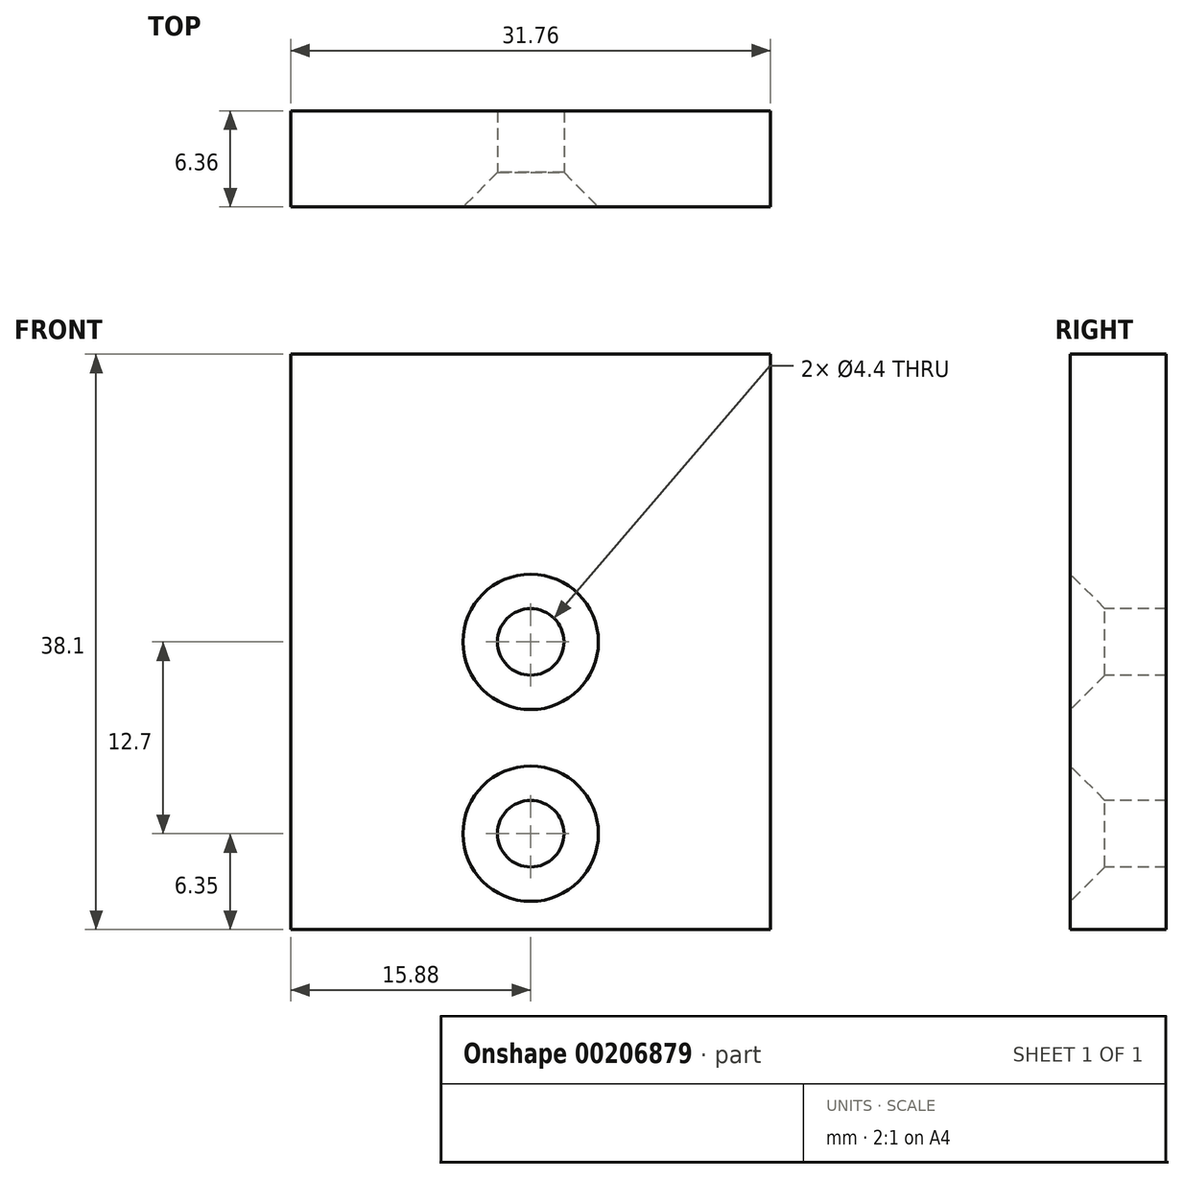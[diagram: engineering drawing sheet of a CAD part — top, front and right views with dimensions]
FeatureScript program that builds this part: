
annotation { "Feature Type Name" : "Feature", "Feature Type Description" : "" }
export const myFeature = defineFeature(function(context is Context, id is Id, definition is map)
    precondition{}
    {
        {
            var Q0;
            Q0=qCreatedBy(makeId("Front.planeOp"),FACE);
            var sketch = newSketch(context, id + "F0", { "sketchPlane" : qUnion([Q0])});
            skLineSegment(sketch, "E0.bottom", {"start": v(-15.87, 19.05) * mm, "end": v(15.88, 19.05) * mm});
            skLineSegment(sketch, "E0.top", {"start": v(-15.88, -19.05) * mm, "end": v(15.87, -19.05) * mm});
            skLineSegment(sketch, "E0.left", {"start": v(-15.87, 19.05) * mm, "end": v(-15.88, -19.05) * mm});
            skLineSegment(sketch, "E0.right", {"start": v(15.88, 19.05) * mm, "end": v(15.87, -19.05) * mm});
            skPoint(sketch, "E0.middle", {"position": v(0, 0) * mm});
            skSolve(sketch);
        }
        {
            var Q0;
            Q0=qSketchRegion(id+"F0",true);
            extrude(context, id + "F1", {"entities" : qUnion([Q0]), "endBound" : BoundingType.SYMMETRIC, "depth" : 6.35 * mm});
        }
        {
            var Q0;
            Q0=makeQuery(id+"F1.opExtrude","CAP_FACE",FACE,{"disambiguationData":[OSD([sQuery(id+"F0.wireOp",EDGE,"E0.bottom"),sQuery(id+"F0.wireOp",EDGE,"E0.top"),sQuery(id+"F0.wireOp",EDGE,"E0.left"),sQuery(id+"F0.wireOp",EDGE,"E0.right")])],"isStart":false});
            var sketch = newSketch(context, id + "F2", { "sketchPlane" : qUnion([Q0])});
            skPoint(sketch, "E1", {"position": v(0, -12.7) * mm});
            skPoint(sketch, "E2", {"position": v(0, 0) * mm});
            skSolve(sketch);
        }
        {
            var Q0;
            Q0=sQuery(id+"F2.wireOp",VERTEX,"E2");
            var Q1;
            Q1=sQuery(id+"F2.wireOp",VERTEX,"E1");
            var Q2;
            Q2=makeQuery(id+"F1.opExtrude","SWEPT_BODY",BODY,{"disambiguationData":[OSD([sQuery(id+"F0.wireOp",EDGE,"E0.bottom"),sQuery(id+"F0.wireOp",EDGE,"E0.top"),sQuery(id+"F0.wireOp",EDGE,"E0.left"),sQuery(id+"F0.wireOp",EDGE,"E0.right")])]});
            hole(context, id + "F3", {"style" : HoleStyle.C_SINK, "endStyle" : HoleEndStyle.BLIND, "standardTappedOrClearance" : lookupTablePath({ "standard" : "ISO", "fit" : "Normal", "size" : "M4", "type" : "Clearance" }), "standardBlindInLast" : lookupTablePath({ "fit" : "Standard", "standard" : "ISO", "size" : "M4", "type" : "Clearance" }), "holeDiameter" : 4.4 * mm, "cSinkDiameter" : 8.96 * mm, "cSinkAngle" : 90 * degree, "holeDepth" : 12.7 * mm, "startFromSketch" : true, "locations" : qUnion([Q0, Q1]), "scope" : qUnion([Q2])});
        }
    });
